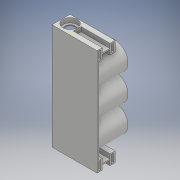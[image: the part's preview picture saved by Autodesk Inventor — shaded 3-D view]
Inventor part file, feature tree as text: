
AUTODESK INVENTOR PART (.ipt)
format: ipt  version: 2018 (Build 220112000, 112)  size: 365,056 bytes
history: native  units: mm
features: sketch x15, extrude x13, fillet x3
ambient origin geometry x8: Origin, YZ Plane, XZ Plane, XY Plane, X Axis, Y Axis, Z Axis, Center Point
bodies: Solid1 (feature_tree)
feature tree (31):
  extrude  "Extrusion1"  Depth=165.0mm
  extrude  "Extrusion2"  Depth=8.5mm
  extrude  "Extrusion3"  Depth=25.0mm TaperAngle=0.0deg
  extrude  "Extrusion4"  Depth=22.75mm
  extrude  "Extrusion5"  Depth=7.1mm
  extrude  "Extrusion6"  Depth=7.1mm TaperAngle=0.0deg
  fillet  "Fillet1"  Radius=5.0mm
  extrude  "Extrusion7"  Depth=10.0mm TaperAngle=0.0deg
  fillet  "Fillet2"  Radius=2.0mm
  extrude  "Extrusion8"  Depth=8.0mm
  extrude  "Extrusion9"  Depth=16.0mm
  fillet  "Fillet3"  Radius=8.0mm
  extrude  "Extrusion10"  Depth=6.0mm
  extrude  "Extrusion11"  Depth=3.5mm
  sketch  "Sketch12"  dims[d32=12.25mm d33=3.5mm]
  sketch  "Sketch13"  dims[d34=12.25mm d35=12.25mm]
  extrude  "Extrusion12"  Depth=3.5mm
  extrude  "Extrusion13"  Depth=12.25mm
  sketch  "Sketch1"  dims[d0=25.0mm d1=165.0mm]
  sketch  "Sketch2"  dims[d2=3.0mm d3=0.0mm d4=8.5mm]
  sketch  "Sketch3"  dims[d5=8.5mm d6=25.0mm d7=0.0mm]
  sketch  "Sketch4"  dims[d8=25.0mm d9=22.75mm]
  sketch  "Sketch5"  dims[d10=7.1mm d11=0.0mm d12=15.5mm]
  sketch  "Sketch6"  dims[d13=165.0mm d14=0.0mm d15=7.1mm d16=0.0mm d17=5.0mm]
  sketch  "Sketch7"  dims[d18=5.0mm d19=10.0mm d20=0.0mm d21=2.0mm]
  sketch  "Sketch8"  dims[d22=16.0mm d23=8.0mm]
  sketch  "Sketch9"  dims[d24=16.0mm d25=16.0mm d26=8.0mm]
  sketch  "Sketch10"  dims[d27=45.0mm d28=0.0mm d29=6.0mm]
  sketch  "Sketch11"  dims[d30=12.25mm d31=3.5mm]
  sketch  "Sketch14"  dims[d36=3.5mm]
  sketch  "Sketch15"  dims[d37=40.0mm d38=0.0mm d39=1.0mm d40=2.0mm d41=8.0mm d42=1.0mm d43=2.0mm d44=12.0mm d45=0.0mm d46=6.0mm d47=7.1mm d48=0.0mm d49=3.0mm d50=0.0mm d51=42.0mm d52=38.75mm d53=42.0mm d54=38.75mm d55=42.0mm d56=38.75mm d57=45.0mm d58=0.0mm d59=2.0mm d60=4.0mm d61=2.0mm d62=4.0mm d63=45.0mm d64=0.0mm]
